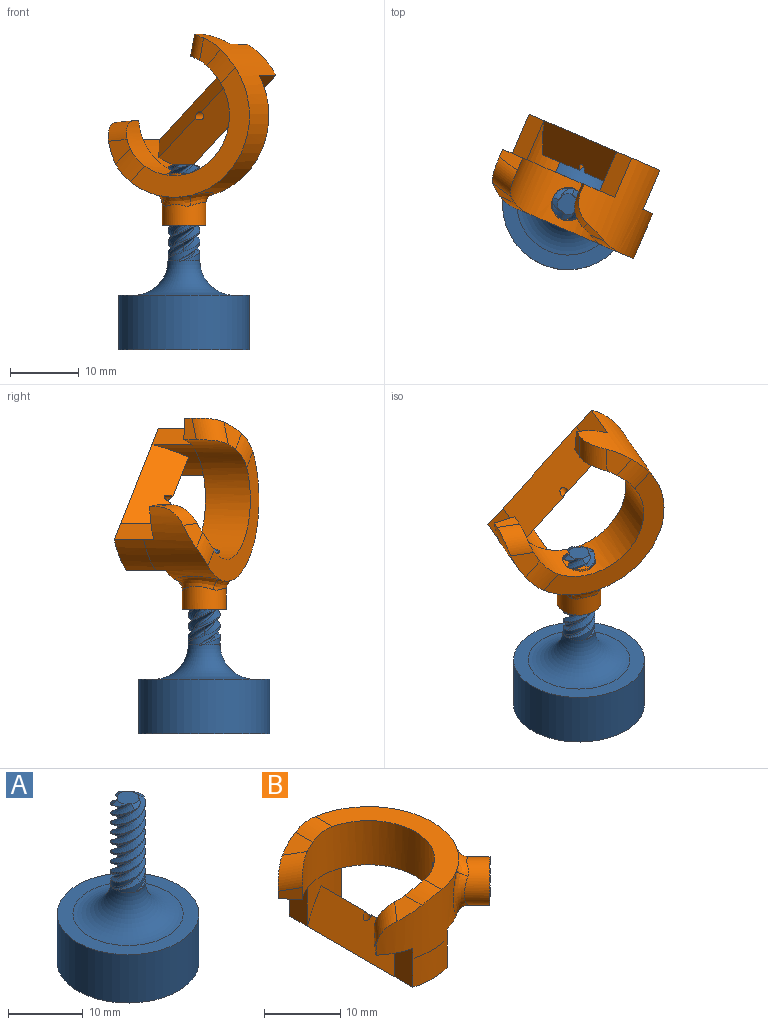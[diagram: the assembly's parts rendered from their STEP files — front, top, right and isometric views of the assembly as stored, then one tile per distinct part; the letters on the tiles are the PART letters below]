
ASSEMBLY  parts=2 mates=1
PART A: 37 faces, bbox 23.9x23.9x28.4 mm
  f0: cylinder r=2.32mm len=13.57mm, axis (0,0,-1), area 8.9mm2, adj f22,f25,f26,f27,f30,f33,f36
  f1: cylinder r=2.32mm len=13.57mm, axis (0,0,-1), area 8.9mm2, adj f14,f15,f18,f28,f31,f32,f36
  f2: cylinder r=2.32mm len=13.57mm, axis (0,0,-1), area 8.9mm2, adj f8,f9,f12,f16,f19,f35,f36
  f3: cylinder r=2.32mm len=13.57mm, axis (0,0,-1), area 8.9mm2, adj f10,f13,f20,f21,f24,f34,f36
  f4: cylinder r=9.53mm len=19.05mm, axis (0,0,-1), area 475mm2, adj f5,f6
  f5: plane 19.05x19.05mm, normal (0,0,1), area 113.1mm2, adj f4,f36
  f6: plane 19.05x19.05mm, normal (0,0,-1), area 285mm2, adj f4
  f7: plane 3.09x3.09mm, normal (0,0,1), area 7mm2, adj f11,f12,f13,f17,f18,f19,f23,f24
  f8: bspline ~4.21x3.14mm, area 2mm2, adj f2,f9,f12
  f9: bspline ~2.94x2.67mm, area 1.5mm2, adj f2,f8,f10,f11,f36
  f10: bspline ~4.39x3.17mm, area 1.8mm2, adj f3,f9,f13,f36
  f11: bspline ~12.6x2.92mm, area 7.8mm2, adj f7,f9,f12,f13
  f12: bspline ~13.2x5.35mm, area 23.2mm2, adj f2,f7,f8,f11,f35
  f13: bspline ~13.2x5.35mm, area 25.1mm2, adj f3,f7,f10,f11,f34
  f14: bspline ~4.21x3.14mm, area 2mm2, adj f1,f15,f18
  f15: bspline ~2.94x2.67mm, area 1.5mm2, adj f1,f14,f16,f17,f36
  f16: bspline ~4.39x3.17mm, area 1.8mm2, adj f2,f15,f19,f36
  f17: bspline ~12.6x2.92mm, area 7.8mm2, adj f7,f15,f18,f19
  f18: bspline ~13.2x5.35mm, area 23.2mm2, adj f1,f7,f14,f17,f32
  f19: bspline ~13.2x5.35mm, area 25.1mm2, adj f2,f7,f16,f17,f35
  f20: bspline ~4.21x3.14mm, area 2mm2, adj f3,f21,f24
  f21: bspline ~2.94x2.67mm, area 1.5mm2, adj f3,f20,f22,f23,f36
  f22: bspline ~4.39x3.17mm, area 1.8mm2, adj f0,f21,f25,f36
  f23: bspline ~12.6x2.92mm, area 7.8mm2, adj f7,f21,f24,f25
  f24: bspline ~13.2x5.35mm, area 23.2mm2, adj f3,f7,f20,f23,f34
  f25: bspline ~13.2x5.35mm, area 25.1mm2, adj f0,f7,f22,f23,f33
  f26: bspline ~4.21x3.14mm, area 2mm2, adj f0,f27,f30
  f27: bspline ~2.94x2.67mm, area 1.5mm2, adj f0,f26,f28,f29,f36
  f28: bspline ~4.39x3.17mm, area 1.8mm2, adj f1,f27,f31,f36
  f29: bspline ~12.6x2.92mm, area 7.8mm2, adj f7,f27,f30,f31
  f30: bspline ~13.2x5.35mm, area 23.2mm2, adj f0,f7,f26,f29,f33
  f31: bspline ~13.2x5.35mm, area 25.1mm2, adj f1,f7,f28,f29,f32
  f32: cone r=2.32mm half-angle=63.4deg, axis (0,0,-1), area 1.1mm2, adj f1,f7,f18,f31
  f33: cone r=2.32mm half-angle=63.4deg, axis (0,0,-1), area 1.1mm2, adj f0,f7,f25,f30
  f34: cone r=2.32mm half-angle=63.4deg, axis (0,0,-1), area 1.1mm2, adj f3,f7,f13,f24
  f35: cone r=2.32mm half-angle=63.4deg, axis (0,0,-1), area 1.1mm2, adj f2,f7,f12,f19
  f36: torus R=7.4mm, axis (0,0,1), area 208.6mm2, adj f0,f1,f2,f3,f5,f9,f10,f15
PART B: 58 faces, bbox 22x26.2x14 mm
  f0: plane 6.22x3.35mm, normal (-1,0,0), area 20.8mm2, adj f6,f10,f52,f53,f54
  f1: plane 6.22x3.35mm, normal (1,0,0), area 20.8mm2, adj f2,f6,f52,f53,f54
  f2: plane 23.18x9mm, normal (0,0,-1), area 82.4mm2, adj f1,f4,f5,f6,f19,f50
  f3: plane 4.82x4.52mm, normal (0,0,-1), area 12.6mm2, adj f4,f5,f8,f49
  f4: cylinder r=8.73mm len=17.46mm, axis (0,0,-1), area 246mm2, adj f2,f3,f7,f8,f9,f10,f11,f12
  f5: cylinder r=11.91mm len=19.56mm, axis (0,0,-1), area 256.3mm2, adj f2,f3,f8,f9,f11,f14,f16,f20
  f6: cylinder r=11.91mm len=13.86mm, axis (0,0,-1), area 93.5mm2, adj f0,f1,f2,f7,f9,f10,f12,f13
  f7: plane 2.43x2.04mm, normal (-0.77,0.64,0), area 5mm2, adj f4,f6,f10,f15
  f8: plane 2.43x2.04mm, normal (-0.77,-0.64,0), area 5mm2, adj f3,f4,f5,f16
  f9: plane 23.74x10.24mm, normal (0,0,1), area 90.8mm2, adj f4,f5,f6,f13,f14,f22
  f10: plane 4.82x4.52mm, normal (0,0,-1), area 12.6mm2, adj f0,f4,f6,f7
  f11: plane 3.69x3.6mm, normal (-0.36,0,0.93), area 9mm2, adj f4,f5,f14,f16
  f12: plane 3.69x3.6mm, normal (-0.36,0,0.93), area 9mm2, adj f4,f6,f13,f15
  f13: cylinder r=10.16mm len=3.67mm, axis (0,-1,0), area 12.1mm2, adj f4,f6,f9,f12
  f14: cylinder r=10.16mm len=3.67mm, axis (0,-1,0), area 12.1mm2, adj f4,f5,f9,f11
  f15: cylinder r=3.81mm len=5.9mm, axis (0.62,0.74,0.24), area 16.4mm2, adj f4,f6,f7,f12
  f16: cylinder r=3.81mm len=5.9mm, axis (-0.62,0.74,-0.24), area 16.4mm2, adj f4,f5,f8,f11
  f17: cylinder r=3.17mm len=6.53mm, axis (-0.71,0.71,0), area 57.6mm2, adj f18,f19,f20,f21,f22
  f18: plane 6.45x4.59mm, normal (0.71,-0.71,0), area 20mm2, adj f17,f23,f24,f25,f26,f27,f28,f29
  f19: bspline ~4.9x4.82mm, area 7.2mm2, adj f2,f17,f20,f21
  f20: bspline ~7.87x3.28mm, area 13.1mm2, adj f5,f17,f19,f22
  f21: bspline ~7.11x2.88mm, area 13.1mm2, adj f6,f17,f19,f22
  f22: bspline ~4.9x4.82mm, area 7.2mm2, adj f9,f17,f20,f21
  f23: bspline ~8.89x7.11mm, area 16mm2, adj f18,f25,f35,f38
  f24: bspline ~8.89x7.11mm, area 16mm2, adj f18,f25,f39,f41
  f25: bspline ~6.61x6.61mm, area 4.2mm2, adj f4,f18,f23,f24,f35,f36,f40,f41
  f26: bspline ~9.77x6.14mm, area 16mm2, adj f18,f28,f39,f41
  f27: bspline ~9.77x6.14mm, area 16mm2, adj f18,f28,f45,f47
  f28: bspline ~9.06x6.32mm, area 4.2mm2, adj f4,f18,f26,f27,f40,f41,f45,f46
  f29: bspline ~9.77x6.14mm, area 16mm2, adj f18,f31,f43,f44
  f30: bspline ~9.77x6.14mm, area 16mm2, adj f18,f31,f35,f38
  f31: bspline ~9.06x6.32mm, area 4.2mm2, adj f4,f18,f29,f30,f35,f37,f42,f43
  f32: bspline ~8.89x7.11mm, area 16mm2, adj f18,f34,f45,f47
  f33: bspline ~8.89x7.11mm, area 16mm2, adj f18,f34,f43,f44
  f34: bspline ~6.61x6.61mm, area 4.2mm2, adj f4,f18,f32,f33,f42,f43,f45,f48
  f35: plane 3.25x0.74mm, normal (-0.71,0.71,0), area 1.6mm2, adj f4,f23,f25,f30,f31,f36,f37,f38
  f36: cylinder r=2.42mm len=0.53mm, axis (0.71,-0.71,0), area 0mm2, adj f4,f25,f35
  f37: cylinder r=2.42mm len=1.55mm, axis (0.71,-0.71,0), area 0.2mm2, adj f4,f31,f35
  f38: cylinder r=1.52mm len=7.52mm, axis (0.71,-0.71,0), area 4.5mm2, adj f18,f23,f30,f35
  f39: cylinder r=1.52mm len=7.52mm, axis (0.71,-0.71,0), area 4.5mm2, adj f18,f24,f26,f41
  f40: cylinder r=2.42mm len=2.5mm, axis (0.71,-0.71,0), area 0.6mm2, adj f4,f25,f28,f41
  f41: plane 2.33x2.33mm, normal (-0.71,0.71,0), area 1.7mm2, adj f24,f25,f26,f28,f39,f40
  f42: cylinder r=2.42mm len=2.5mm, axis (0.71,-0.71,0), area 0.6mm2, adj f4,f31,f34,f43
  f43: plane 2.33x2.33mm, normal (-0.71,0.71,0), area 1.7mm2, adj f29,f31,f33,f34,f42,f44
  f44: cylinder r=1.52mm len=7.52mm, axis (0.71,-0.71,0), area 4.5mm2, adj f18,f29,f33,f43
  f45: plane 3.25x0.74mm, normal (-0.71,0.71,0), area 1.6mm2, adj f4,f27,f28,f32,f34,f46,f47,f48
  f46: cylinder r=2.42mm len=1.55mm, axis (0.71,-0.71,0), area 0.2mm2, adj f4,f28,f45
  f47: cylinder r=1.52mm len=7.52mm, axis (0.71,-0.71,0), area 4.5mm2, adj f18,f27,f32,f45
  f48: cylinder r=2.42mm len=0.53mm, axis (0.71,-0.71,0), area 0mm2, adj f4,f34,f45
  f49: plane 6.22x3.34mm, normal (-1,0,0), area 20.8mm2, adj f3,f5,f51,f54
  f50: plane 6.22x3.34mm, normal (1,0,0), area 20.8mm2, adj f2,f5,f51,f54
  f51: cylinder r=8.74mm len=6.35mm, axis (0,0,1), area 25.6mm2, adj f4,f49,f50,f54,f55,f56
  f52: cylinder r=8.74mm len=6.35mm, axis (0,0,1), area 25.6mm2, adj f0,f1,f4,f54,f55,f56
  f53: cylinder r=11.91mm len=6.35mm, axis (0,0,1), area 29.8mm2, adj f0,f1,f6,f54
  f54: plane 23.82x6.35mm, normal (0,0,-1), area 148.1mm2, adj f0,f1,f5,f49,f50,f51,f52,f53
  f55: plane 17.87x5.03mm, normal (-0.83,0,0.56), area 94.9mm2, adj f51,f52,f54,f56,f57
  f56: plane 17.48x4.64mm, normal (0.83,0,0.56), area 94.9mm2, adj f51,f52,f54,f55,f57
  f57: cylinder r=0.64mm len=4.64mm, axis (0,0,-1), area 16.4mm2, adj f54,f55,f56
PLACE A rot(axis=(0,1,0),0deg) t=(0.62,-1.02,0.03)mm fixed
PLACE B rot(axis=(0.86,0.16,-0.49),108.3deg) t=(2.02,2.25,34.15)mm
MATE cylindrical B.f17 <-> A.f4  axis (0,0,1) through (0.62,-1.02,19.86)mm
